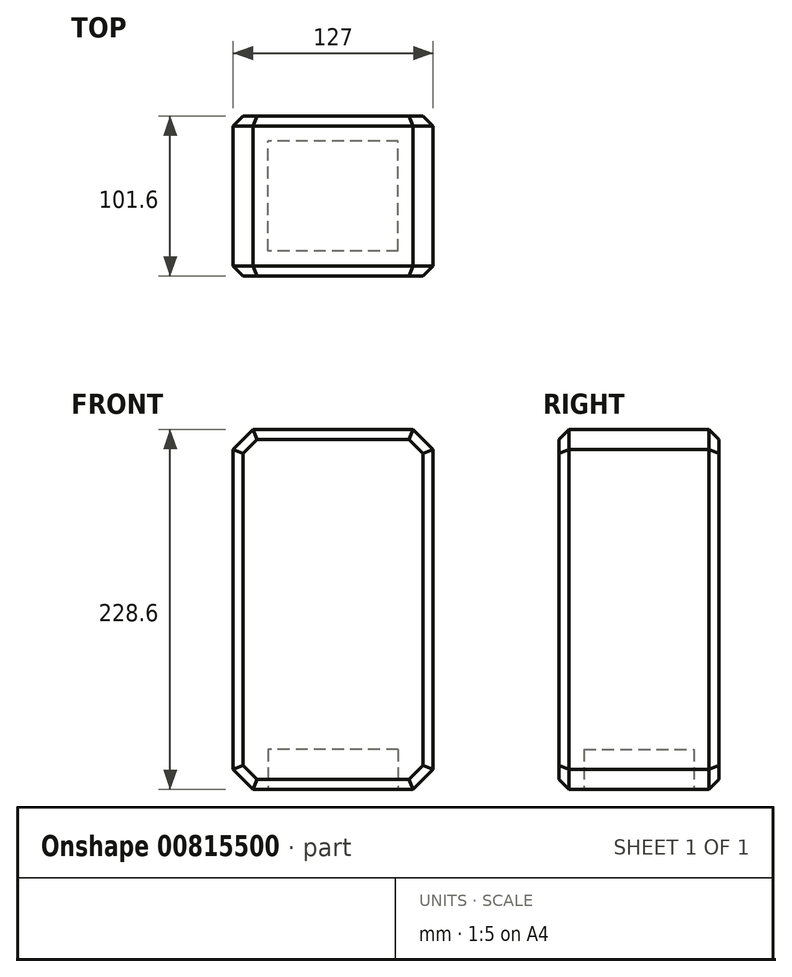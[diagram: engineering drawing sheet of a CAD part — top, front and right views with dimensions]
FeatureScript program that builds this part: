
annotation { "Feature Type Name" : "Feature", "Feature Type Description" : "" }
export const myFeature = defineFeature(function(context is Context, id is Id, definition is map)
    precondition{}
    {
        {
            var Q0;
            Q0=qCreatedBy(makeId("Front.planeOp"),FACE);
            var sketch = newSketch(context, id + "F0", { "sketchPlane" : qUnion([Q0])});
            skLineSegment(sketch, "E0.bottom", {"start": v(63.5, -114.3) * mm, "end": v(-63.5, -114.3) * mm});
            skLineSegment(sketch, "E0.top", {"start": v(63.5, 114.3) * mm, "end": v(-63.5, 114.3) * mm});
            skLineSegment(sketch, "E0.left", {"start": v(63.5, -114.3) * mm, "end": v(63.5, 114.3) * mm});
            skLineSegment(sketch, "E0.right", {"start": v(-63.5, -114.3) * mm, "end": v(-63.5, 114.3) * mm});
            skPoint(sketch, "E0.middle", {"position": v(0, 0) * mm});
            skSolve(sketch);
        }
        {
            var Q0;
            Q0 = qSketchRegion(id + "F0", true);
            extrude(context, id + "F1", {"entities" : qUnion([Q0]), "endBound" : BoundingType.SYMMETRIC, "depth" : 101.6 * mm, "offsetDistance" : 25.4 * mm});
        }
        {
            var Q0;
            Q0=makeQuery(id+"F1.opExtrude","SWEPT_EDGE",EDGE,{"disambiguationData":[OSD([sQuery(id+"F0.wireOp",EDGE,"E0.top"),sQuery(id+"F0.wireOp",EDGE,"E0.right")])]});
            var Q1;
            Q1=makeQuery(id+"F1.opExtrude","SWEPT_EDGE",EDGE,{"disambiguationData":[OSD([sQuery(id+"F0.wireOp",EDGE,"E0.top"),sQuery(id+"F0.wireOp",EDGE,"E0.left")])]});
            var Q2;
            Q2=makeQuery(id+"F1.opExtrude","SWEPT_EDGE",EDGE,{"disambiguationData":[OSD([sQuery(id+"F0.wireOp",EDGE,"E0.bottom"),sQuery(id+"F0.wireOp",EDGE,"E0.left")])]});
            var Q3;
            Q3=makeQuery(id+"F1.opExtrude","SWEPT_EDGE",EDGE,{"disambiguationData":[OSD([sQuery(id+"F0.wireOp",EDGE,"E0.bottom"),sQuery(id+"F0.wireOp",EDGE,"E0.right")])]});
            chamfer(context, id + "F2", {"entities" : qUnion([Q0, Q1, Q2, Q3]), "width" : 12.7 * mm, "tangentPropagation" : true});
        }
        {
            var Q0;
            Q0=makeQuery(id+"F1.opExtrude","CAP_FACE",FACE,{"disambiguationData":[OSD([sQuery(id+"F0.wireOp",EDGE,"E0.bottom"),sQuery(id+"F0.wireOp",EDGE,"E0.top"),sQuery(id+"F0.wireOp",EDGE,"E0.left"),sQuery(id+"F0.wireOp",EDGE,"E0.right")])],"isStart":false});
            var Q1;
            Q1=makeQuery(id+"F1.opExtrude","CAP_FACE",FACE,{"disambiguationData":[OSD([sQuery(id+"F0.wireOp",EDGE,"E0.bottom"),sQuery(id+"F0.wireOp",EDGE,"E0.top"),sQuery(id+"F0.wireOp",EDGE,"E0.left"),sQuery(id+"F0.wireOp",EDGE,"E0.right")])],"isStart":true});
            chamfer(context, id + "F3", {"entities" : qUnion([Q0, Q1]), "width" : 6.35 * mm, "tangentPropagation" : true});
        }
        {
            var Q0;
            Q0=makeQuery(id+"F1.opExtrude","SWEPT_FACE",FACE,{"disambiguationData":[OSD([sQuery(id+"F0.wireOp",EDGE,"E0.bottom")])]});
            var sketch = newSketch(context, id + "F4", { "sketchPlane" : qUnion([Q0])});
            skLineSegment(sketch, "E1.bottom", {"start": v(41.28, 34.93) * mm, "end": v(-41.27, 34.93) * mm});
            skLineSegment(sketch, "E1.top", {"start": v(41.28, -34.93) * mm, "end": v(-41.27, -34.93) * mm});
            skLineSegment(sketch, "E1.left", {"start": v(41.28, 34.93) * mm, "end": v(41.28, -34.93) * mm});
            skLineSegment(sketch, "E1.right", {"start": v(-41.28, 34.93) * mm, "end": v(-41.28, -34.93) * mm});
            skPoint(sketch, "E1.middle", {"position": v(0, 0) * mm});
            skSolve(sketch);
        }
        {
            var Q0;
            Q0 = qSketchRegion(id + "F4", true);
            extrude(context, id + "F5", {"entities" : qUnion([Q0]), "operationType" : NewBodyOperationType.REMOVE, "oppositeDirection" : true, "depth" : 25.4 * mm, "offsetDistance" : 25.4 * mm});
        }
    });
